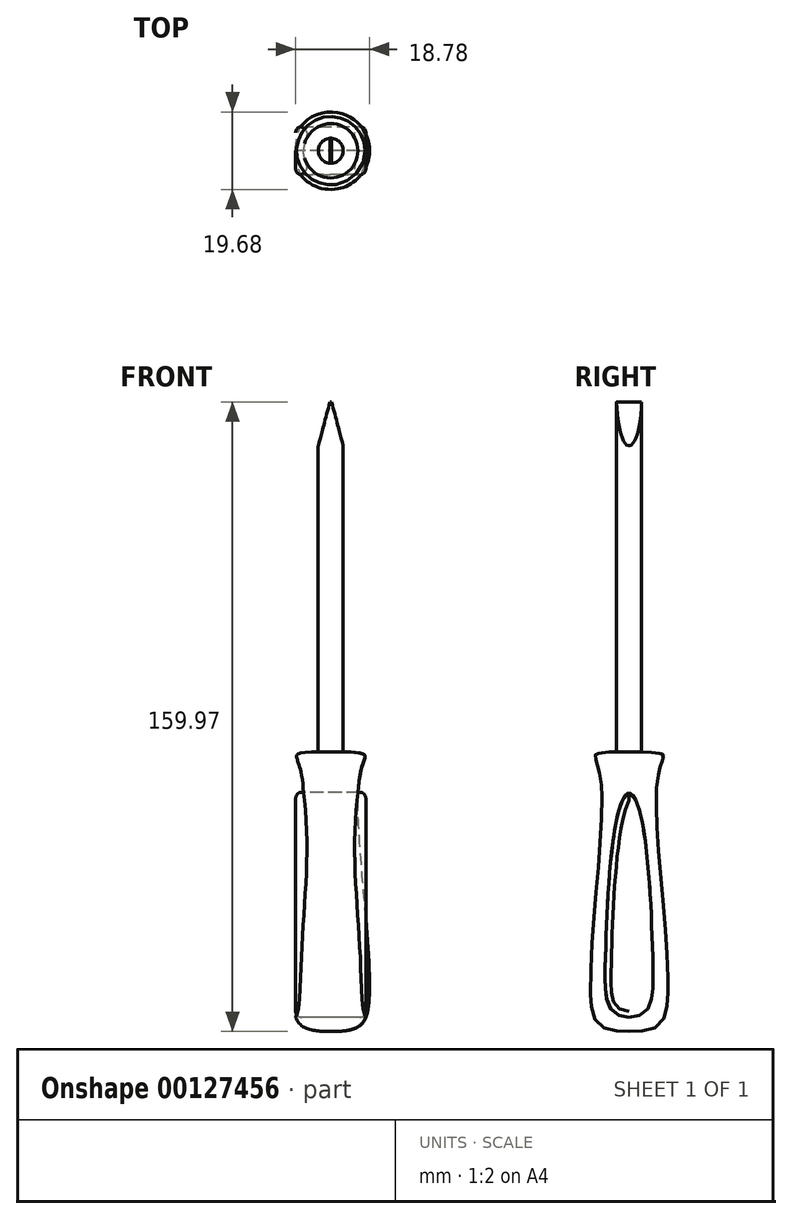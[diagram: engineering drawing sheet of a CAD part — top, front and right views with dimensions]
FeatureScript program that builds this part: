
annotation { "Feature Type Name" : "Feature", "Feature Type Description" : "" }
export const myFeature = defineFeature(function(context is Context, id is Id, definition is map)
    precondition{}
    {
        {
            var Q0;
            Q0=qCreatedBy(makeId("Front.planeOp"),FACE);
            var sketch = newSketch(context, id + "F0", { "sketchPlane" : qUnion([Q0])});
            skFitSpline(sketch, "E0", {"points": [v(0, -43.12) * mm, v(9.68, -35.74) * mm, v(6.98, 18.51) * mm, v(8.63, 26.4) * mm, v(0, 27.95) * mm], "startDerivative": vector(106.65, 0) * mm, "endDerivative": vector(-141.07, 0) * mm});
            skLineSegment(sketch, "E1", {"start": v(0, 39.2) * mm, "end": v(0, -52.53) * mm, "construction": true});
            skLineSegment(sketch, "E2", {"start": v(0, 27.95) * mm, "end": v(0, -43.12) * mm});
            skSolve(sketch);
        }
        {
            var Q0;
            Q0=makeQuery(id+"F0.imprint","IMPRINT",FACE,{"disambiguationData":[TD([[makeQuery(id+"F0.imprint","IMPRINT",EDGE,{"derivedFrom":sQuery(id+"F0.wireOp",EDGE,"E0")}),1.0]])]});
            var Q1;
            Q1=sQuery(id+"F0.wireOp",EDGE,"E1");
            revolve(context, id + "F1", {"entities" : qUnion([Q0]), "axis" : qUnion([Q1]), "revolveType" : RevolveType.FULL});
        }
        {
            var Q0;
            Q0=qCreatedBy(makeId("Top.planeOp"),FACE);
            var Q1;
            {var subQ0=sQuery(id+"F0.wireOp",EDGE,"E0");var subQ1=sQuery(id+"F0.wireOp",EDGE,"E2");Q1=makeQuery(id+"F1.opRevolve","SWEPT_VERTEX",VERTEX,{"disambiguationData":[OSD([subQ0,subQ1]),TDD([makeQuery(id+"F0.imprint","INTERSECT",VERTEX,{"disambiguationData":[OD(1.0)],"derivedFrom":[subQ0,subQ1]})])]});}
            cPlane(context, id + "F2", {"entities" : qUnion([Q0, Q1]), "cplaneType" : CPlaneType.PLANE_POINT, "offset" : 152.4 * mm, "width" : 152.4 * mm, "height" : 152.4 * mm});
        }
        {
            var Q0;
            Q0=qCreatedBy(id+"F2.planeOp",FACE);
            var sketch = newSketch(context, id + "F3", { "sketchPlane" : qUnion([Q0])});
            skCircle(sketch, "E3", {"center": v(0, 0) * mm, "radius": 3.18 * mm});
            skSolve(sketch);
        }
        {
            var Q0;
            Q0=makeQuery(id+"F3.imprint","IMPRINT",FACE,{"disambiguationData":[TD([[makeQuery(id+"F3.imprint","IMPRINT",EDGE,{"derivedFrom":sQuery(id+"F3.wireOp",EDGE,"E3")}),1.0]])]});
            extrude(context, id + "F4", {"entities" : qUnion([Q0]), "depth" : 88.9 * mm});
        }
        {
            var Q0;
            Q0=qCreatedBy(makeId("Front.planeOp"),FACE);
            var sketch = newSketch(context, id + "F5", { "sketchPlane" : qUnion([Q0])});
            skLineSegment(sketch, "E4", {"start": v(-0.21, 116.85) * mm, "end": v(-3.58, 104.15) * mm});
            skLineSegment(sketch, "E5", {"start": v(-3.58, 116.85) * mm, "end": v(-0.21, 116.85) * mm});
            skLineSegment(sketch, "E6", {"start": v(-3.58, 116.85) * mm, "end": v(-3.58, 104.15) * mm});
            skLineSegment(sketch, "E7", {"start": v(0, 101.18) * mm, "end": v(0, 83.15) * mm, "construction": true});
            skLineSegment(sketch, "E8.0.MirrorCS", {"start": v(3.58, 116.85) * mm, "end": v(3.58, 104.15) * mm});
            skLineSegment(sketch, "E8.1.MirrorCS", {"start": v(0.21, 116.85) * mm, "end": v(3.58, 104.15) * mm});
            skLineSegment(sketch, "E8.2.MirrorCS", {"start": v(3.58, 116.85) * mm, "end": v(0.21, 116.85) * mm});
            skSolve(sketch);
        }
        {
            var Q0;
            Q0=makeQuery(id+"F5.imprint","IMPRINT",FACE,{"disambiguationData":[TD([[makeQuery(id+"F5.imprint","IMPRINT",EDGE,{"derivedFrom":sQuery(id+"F5.wireOp",EDGE,"E4")}),-1.0]])]});
            var Q1;
            Q1=makeQuery(id+"F5.imprint","IMPRINT",FACE,{"disambiguationData":[TD([[makeQuery(id+"F5.imprint","IMPRINT",EDGE,{"derivedFrom":sQuery(id+"F5.wireOp",EDGE,"E8.0.MirrorCS")}),-1.0]])]});
            extrude(context, id + "F6", {"entities" : qUnion([Q0, Q1]), "operationType" : NewBodyOperationType.REMOVE, "endBound" : BoundingType.SYMMETRIC, "oppositeDirection" : true, "depth" : 25.4 * mm});
        }
        {
            var Q0;
            Q0=qCreatedBy(makeId("Right.planeOp"),FACE);
            var sketch = newSketch(context, id + "F7", { "sketchPlane" : qUnion([Q0])});
            skFitSpline(sketch, "E9", {"points": [v(0, 17.7) * mm, v(-6, -23.84) * mm, v(-4.27, -37.87) * mm, v(0, -39.47) * mm], "startDerivative": vector(-25.93, -10.75) * mm, "endDerivative": vector(24.5, 0) * mm});
            skLineSegment(sketch, "E10", {"start": v(0, -43.83) * mm, "end": v(0, 22.96) * mm, "construction": true});
            skFitSpline(sketch, "E11.0.MirrorCS", {"points": [v(0, 17.7) * mm, v(6, -23.84) * mm, v(4.27, -37.87) * mm, v(0, -39.47) * mm], "startDerivative": vector(25.93, -10.75) * mm, "endDerivative": vector(-24.5, 0) * mm});
            skSolve(sketch);
        }
        {
            var Q0;
            Q0=makeQuery(id+"F7.imprint","IMPRINT",FACE,{"disambiguationData":[TD([[makeQuery(id+"F7.imprint","IMPRINT",EDGE,{"derivedFrom":sQuery(id+"F7.wireOp",EDGE,"E9")}),1.0]])]});
            extrude(context, id + "F8", {"entities" : qUnion([Q0]), "operationType" : NewBodyOperationType.REMOVE, "endBound" : BoundingType.SYMMETRIC, "depth" : 22.52 * mm});
        }
        {
            var Q0;
            Q0=makeQuery(id+"F7.imprint","IMPRINT",FACE,{"disambiguationData":[TD([[makeQuery(id+"F7.imprint","IMPRINT",EDGE,{"derivedFrom":sQuery(id+"F7.wireOp",EDGE,"E9")}),1.0]])]});
            var Q1;
            Q1=makeQuery(id+"F1.opRevolve","SWEPT_BODY",BODY,{"disambiguationData":[OSD([sQuery(id+"F0.wireOp",EDGE,"E0"),sQuery(id+"F0.wireOp",EDGE,"E2")])]});
            extrude(context, id + "F9", {"entities" : qUnion([Q0]), "endBound" : BoundingType.SYMMETRIC, "endBoundEntity" : qUnion([Q1]), "depth" : 17.87 * mm});
        }
        {
            var Q0;
            Q0=makeQuery(id+"F9.opExtrude","CAP_EDGE",EDGE,{"disambiguationData":[OSD([sQuery(id+"F7.wireOp",EDGE,"E9")])],"isStart":false});
            var Q1;
            Q1=makeQuery(id+"F9.opExtrude","CAP_EDGE",EDGE,{"disambiguationData":[OSD([sQuery(id+"F7.wireOp",EDGE,"E9")])],"isStart":true});
            fillet(context, id + "F10", {"entities" : qUnion([Q0, Q1]), "radius" : 1.52 * mm, "tangentPropagation" : true, "allowEdgeOverflow" : false});
        }
    });
